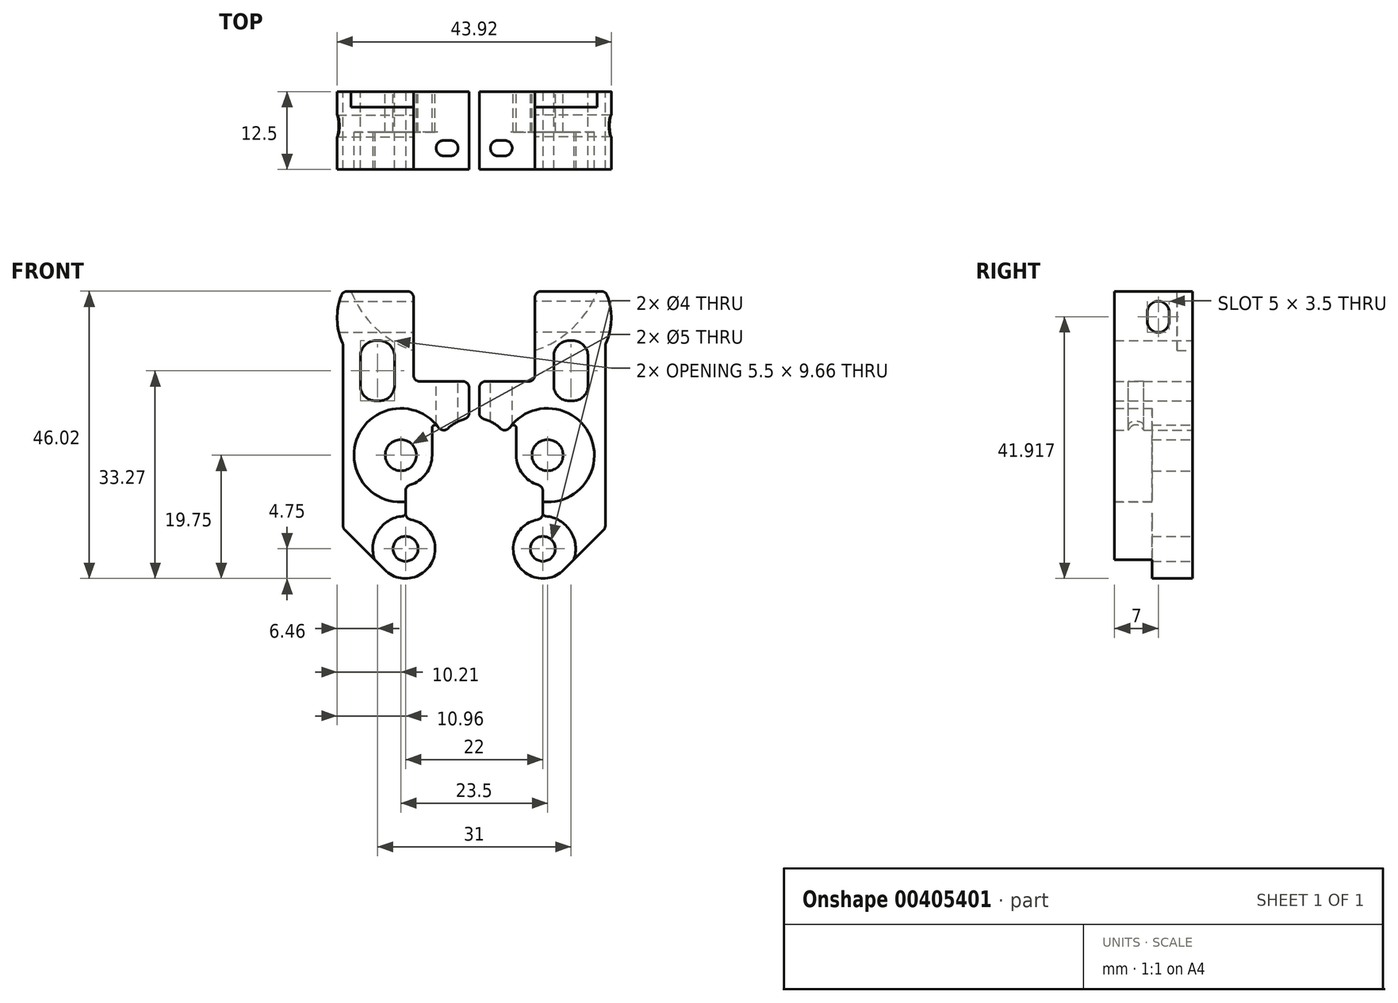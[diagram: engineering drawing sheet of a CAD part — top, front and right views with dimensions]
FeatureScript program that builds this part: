
annotation { "Feature Type Name" : "Feature", "Feature Type Description" : "" }
export const myFeature = defineFeature(function(context is Context, id is Id, definition is map)
    precondition{}
    {
        {
            var Q0;
            Q0=qCreatedBy(makeId("Front.planeOp"),FACE);
            var sketch = newSketch(context, id + "F0", { "sketchPlane" : qUnion([Q0])});
            skArc(sketch, "E0", {"start": v(6.75, 0) * mm, "mid": v(7.96, -3.26) * mm, "end": v(11, -4.94) * mm});
            skLineSegment(sketch, "E1", {"start": v(11, -4.94) * mm, "end": v(11, -10.25) * mm});
            skCircle(sketch, "E2", {"center": v(11, -15) * mm, "radius": 2 * mm});
            skArc(sketch, "E3.converted", {"start": v(11, -10.25) * mm, "mid": v(6.61, -16.82) * mm, "end": v(14.36, -18.36) * mm});
            skCircle(sketch, "E4", {"center": v(11.75, 0) * mm, "radius": 2.5 * mm});
            skPoint(sketch, "E5", {"position": v(15.5, 15.5) * mm});
            skCircle(sketch, "E6", {"center": v(15.5, 15.5) * mm, "radius": 2 * mm, "construction": true});
            skLineSegment(sketch, "E7", {"start": v(9.72, 26.27) * mm, "end": v(9.72, 11.81) * mm});
            skLineSegment(sketch, "E8", {"start": v(21, 17.74) * mm, "end": v(21, -11.72) * mm});
            skLineSegment(sketch, "E9", {"start": v(12.75, 18.35) * mm, "end": v(12.75, 8.7) * mm});
            skLineSegment(sketch, "E10", {"start": v(12.75, 8.7) * mm, "end": v(18.25, 8.7) * mm});
            skLineSegment(sketch, "E11", {"start": v(18.25, 18.35) * mm, "end": v(18.25, 8.7) * mm});
            skLineSegment(sketch, "E12", {"start": v(14.36, -18.36) * mm, "end": v(21, -11.72) * mm});
            skLineSegment(sketch, "E13", {"start": v(9.72, 26.27) * mm, "end": v(21, 26.27) * mm});
            skCircle(sketch, "E14", {"center": v(0, 0) * mm, "radius": 3.5 * mm, "construction": true});
            skLineSegment(sketch, "E15", {"start": v(4.38, 17.47) * mm, "end": v(4.38, -21.47) * mm, "construction": true});
            skLineSegment(sketch, "E16", {"start": v(3.5, 6.48) * mm, "end": v(3.5, -16.85) * mm, "construction": true});
            skLineSegment(sketch, "E17", {"start": v(5.25, 6.48) * mm, "end": v(5.25, -16.85) * mm, "construction": true});
            skLineSegment(sketch, "E18", {"start": v(0, 24.67) * mm, "end": v(0, -21.27) * mm, "construction": true});
            skLineSegment(sketch, "E19", {"start": v(0, 0) * mm, "end": v(23.5, 0) * mm, "construction": true});
            skLineSegment(sketch, "E20", {"start": v(0.79, -15) * mm, "end": v(15, -15) * mm, "construction": true});
            skCircle(sketch, "E21", {"center": v(11.75, 0) * mm, "radius": 6.5 * mm, "construction": true});
            skLineSegment(sketch, "E22", {"start": v(12.75, 18.35) * mm, "end": v(18.25, 18.35) * mm});
            skLineSegment(sketch, "E23", {"start": v(15.5, 24.97) * mm, "end": v(15.5, 6.97) * mm, "construction": true});
            skArc(sketch, "E24", {"start": v(21, 17.74) * mm, "mid": v(21.96, 22) * mm, "end": v(21, 26.27) * mm});
            skLineSegment(sketch, "E25", {"start": v(0.8, 5.95) * mm, "end": v(0.8, 11.81) * mm});
            skLineSegment(sketch, "E26", {"start": v(0.8, 11.81) * mm, "end": v(9.72, 11.81) * mm});
            skArc(sketch, "E27", {"start": v(5.01, 3.3) * mm, "mid": v(3.2, 5.08) * mm, "end": v(0.8, 5.95) * mm});
            skArc(sketch, "E28", {"start": v(6.75, 5.6) * mm, "mid": v(5.77, 4.53) * mm, "end": v(5.01, 3.3) * mm});
            skLineSegment(sketch, "E29.trimOffspring", {"start": v(6.75, 5.6) * mm, "end": v(6.75, 0) * mm});
            skSolve(sketch);
        }
        {
            var Q0;
            Q0=makeQuery(id+"F0.imprint","IMPRINT",FACE,{"disambiguationData":[TD([[makeQuery(id+"F0.imprint","IMPRINT",EDGE,{"derivedFrom":sQuery(id+"F0.wireOp",EDGE,"E0")}),1.0]])]});
            extrude(context, id + "F1", {"entities" : qUnion([Q0]), "depth" : 12.5 * mm});
        }
        {
            var Q0;
            Q0=qCreatedBy(makeId("Front.planeOp"),FACE);
            var sketch = newSketch(context, id + "F2", { "sketchPlane" : qUnion([Q0])});
            skLineSegment(sketch, "E30", {"start": v(9.72, 26.27) * mm, "end": v(19.72, 26.27) * mm});
            skLineSegment(sketch, "E31", {"start": v(9.72, 26.27) * mm, "end": v(9.72, 16.77) * mm});
            skArc(sketch, "E32", {"start": v(9.72, 16.77) * mm, "mid": v(15.8, 20.38) * mm, "end": v(19.72, 26.27) * mm});
            skSolve(sketch);
        }
        {
            var Q0;
            Q0=qSketchRegion(id+"F2",true);
            extrude(context, id + "F3", {"entities" : qUnion([Q0]), "operationType" : NewBodyOperationType.REMOVE, "depth" : 2.5 * mm});
        }
        {
            var Q0;
            Q0=makeQuery(id+"F1.opExtrude","SWEPT_FACE",FACE,{"disambiguationData":[OSD([sQuery(id+"F0.wireOp",EDGE,"E7")])]});
            var sketch = newSketch(context, id + "F4", { "sketchPlane" : qUnion([Q0])});
            skArc(sketch, "E33", {"start": v(3.75, 21.42) * mm, "mid": v(5.5, 19.67) * mm, "end": v(7.25, 21.42) * mm});
            skArc(sketch, "E34", {"start": v(7.25, 22.92) * mm, "mid": v(5.5, 24.67) * mm, "end": v(3.75, 22.92) * mm});
            skLineSegment(sketch, "E35", {"start": v(3.75, 22.92) * mm, "end": v(3.75, 21.42) * mm});
            skLineSegment(sketch, "E36", {"start": v(7.25, 22.92) * mm, "end": v(7.25, 21.42) * mm});
            skSolve(sketch);
        }
        {
            var Q0;
            Q0=qSketchRegion(id+"F4",true);
            extrude(context, id + "F5", {"entities" : qUnion([Q0]), "operationType" : NewBodyOperationType.REMOVE, "endBound" : BoundingType.THROUGH_ALL, "oppositeDirection" : true, "depth" : 25 * mm});
        }
        {
            var Q0;
            Q0=makeQuery(id+"F1.opExtrude","CAP_FACE",FACE,{"disambiguationData":[OSD([sQuery(id+"F0.wireOp",EDGE,"E0"),sQuery(id+"F0.wireOp",EDGE,"E1"),sQuery(id+"F0.wireOp",EDGE,"E2"),sQuery(id+"F0.wireOp",EDGE,"E3.converted"),sQuery(id+"F0.wireOp",EDGE,"E4"),sQuery(id+"F0.wireOp",EDGE,"OX34bXYy-n6Dd-ew0i-KdsQ-qNI713Miu0u2"),sQuery(id+"F0.wireOp",EDGE,"C01J1Lxy-QLMX-vXtg-QGuS-nqejL01fxZ92"),sQuery(id+"F0.wireOp",EDGE,"RrzfEigL-hX7B-k2Xl-mGOe-frZWyb8J06Is"),sQuery(id+"F0.wireOp",EDGE,"E7"),sQuery(id+"F0.wireOp",EDGE,"E8"),sQuery(id+"F0.wireOp",EDGE,"E9"),sQuery(id+"F0.wireOp",EDGE,"E10"),sQuery(id+"F0.wireOp",EDGE,"E11"),sQuery(id+"F0.wireOp",EDGE,"E12"),sQuery(id+"F0.wireOp",EDGE,"E13")])],"isStart":false});
            var sketch = newSketch(context, id + "F6", { "sketchPlane" : qUnion([Q0])});
            skLineSegment(sketch, "E37", {"start": v(9.72, 26.27) * mm, "end": v(9.72, 26.27) * mm});
            skArc(sketch, "E38", {"start": v(6.75, 5.6) * mm, "mid": v(18.88, 2.32) * mm, "end": v(11, -7.46) * mm});
            skArc(sketch, "E39", {"start": v(11, -9.75) * mm, "mid": v(15.3, -11.98) * mm, "end": v(15.94, -16.78) * mm});
            skLineSegment(sketch, "E40", {"start": v(11, -7.46) * mm, "end": v(11, -4.94) * mm});
            skLineSegment(sketch, "E41", {"start": v(6.75, 5.6) * mm, "end": v(6.75, 0) * mm});
            skArc(sketch, "E42", {"start": v(6.75, 0) * mm, "mid": v(7.96, -3.26) * mm, "end": v(11, -4.94) * mm});
            skLineSegment(sketch, "E43", {"start": v(11, -9.75) * mm, "end": v(11, -10.25) * mm});
            skLineSegment(sketch, "E44", {"start": v(15.94, -16.78) * mm, "end": v(14.36, -18.36) * mm});
            skArc(sketch, "E45", {"start": v(11, -10.25) * mm, "mid": v(6.61, -16.82) * mm, "end": v(14.36, -18.36) * mm});
            skSolve(sketch);
        }
        {
            var Q0;
            Q0=qSketchRegion(id+"F6",true);
            extrude(context, id + "F7", {"entities" : qUnion([Q0]), "operationType" : NewBodyOperationType.REMOVE, "oppositeDirection" : true, "depth" : 6 * mm});
        }
        {
            var Q0;
            Q0=makeQuery(id+"F1.opExtrude","SWEPT_FACE",FACE,{"disambiguationData":[OSD([sQuery(id+"F0.wireOp",EDGE,"E26")])]});
            var sketch = newSketch(context, id + "F8", { "sketchPlane" : qUnion([Q0])});
            skArc(sketch, "E46", {"start": v(3.84, -7.82) * mm, "mid": v(2.6, -9.07) * mm, "end": v(3.84, -10.32) * mm});
            skArc(sketch, "E47", {"start": v(4.84, -10.32) * mm, "mid": v(6.1, -9.07) * mm, "end": v(4.84, -7.82) * mm});
            skLineSegment(sketch, "E48", {"start": v(3.84, -7.82) * mm, "end": v(4.84, -7.82) * mm});
            skLineSegment(sketch, "E49", {"start": v(3.84, -10.32) * mm, "end": v(4.84, -10.32) * mm});
            skSolve(sketch);
        }
        {
            var Q0;
            Q0=qSketchRegion(id+"F8",true);
            extrude(context, id + "F9", {"entities" : qUnion([Q0]), "operationType" : NewBodyOperationType.REMOVE, "endBound" : BoundingType.UP_TO_NEXT, "oppositeDirection" : true, "depth" : 25 * mm});
        }
        {
            var Q0;
            Q0=makeQuery(id+"F1.opExtrude","SWEPT_BODY",BODY,{"disambiguationData":[OSD([sQuery(id+"F0.wireOp",EDGE,"E0"),sQuery(id+"F0.wireOp",EDGE,"E1"),sQuery(id+"F0.wireOp",EDGE,"E2"),sQuery(id+"F0.wireOp",EDGE,"E3.converted"),sQuery(id+"F0.wireOp",EDGE,"E4"),sQuery(id+"F0.wireOp",EDGE,"E7"),sQuery(id+"F0.wireOp",EDGE,"E8"),sQuery(id+"F0.wireOp",EDGE,"E9"),sQuery(id+"F0.wireOp",EDGE,"E10"),sQuery(id+"F0.wireOp",EDGE,"E11"),sQuery(id+"F0.wireOp",EDGE,"E12"),sQuery(id+"F0.wireOp",EDGE,"E13"),sQuery(id+"F0.wireOp",EDGE,"E22")])]});
            var Q1;
            Q1=qCreatedBy(makeId("Right.planeOp"),FACE);
            mirror(context, id + "F10", {"entities" : qUnion([Q0]), "mirrorPlane" : qUnion([Q1])});
        }
        {
            var Q0;
            Q0=makeQuery(id+"F1.opExtrude","SWEPT_EDGE",EDGE,{"disambiguationData":[OSD([sQuery(id+"F0.wireOp",EDGE,"E10"),sQuery(id+"F0.wireOp",EDGE,"E11")])]});
            var Q1;
            Q1=makeQuery(id+"F1.opExtrude","SWEPT_EDGE",EDGE,{"disambiguationData":[OSD([sQuery(id+"F0.wireOp",EDGE,"E9"),sQuery(id+"F0.wireOp",EDGE,"E10")])]});
            var Q2;
            Q2=makeQuery(id+"F1.opExtrude","SWEPT_EDGE",EDGE,{"disambiguationData":[OSD([sQuery(id+"F0.wireOp",EDGE,"E9"),sQuery(id+"F0.wireOp",EDGE,"E22")])]});
            var Q3;
            Q3=makeQuery(id+"F1.opExtrude","SWEPT_EDGE",EDGE,{"disambiguationData":[OSD([sQuery(id+"F0.wireOp",EDGE,"E11"),sQuery(id+"F0.wireOp",EDGE,"E22")])]});
            var Q4;
            Q4=makeQuery(id+"F10.opPattern","COPY",EDGE,{"derivedFrom":makeQuery(id+"F1.opExtrude","SWEPT_EDGE",EDGE,{"disambiguationData":[OSD([sQuery(id+"F0.wireOp",EDGE,"E11"),sQuery(id+"F0.wireOp",EDGE,"E22")])]}),"instanceName":"1"});
            var Q5;
            Q5=makeQuery(id+"F10.opPattern","COPY",EDGE,{"derivedFrom":makeQuery(id+"F1.opExtrude","SWEPT_EDGE",EDGE,{"disambiguationData":[OSD([sQuery(id+"F0.wireOp",EDGE,"E9"),sQuery(id+"F0.wireOp",EDGE,"E22")])]}),"instanceName":"1"});
            var Q6;
            Q6=makeQuery(id+"F10.opPattern","COPY",EDGE,{"derivedFrom":makeQuery(id+"F1.opExtrude","SWEPT_EDGE",EDGE,{"disambiguationData":[OSD([sQuery(id+"F0.wireOp",EDGE,"E10"),sQuery(id+"F0.wireOp",EDGE,"E11")])]}),"instanceName":"1"});
            var Q7;
            Q7=makeQuery(id+"F10.opPattern","COPY",EDGE,{"derivedFrom":makeQuery(id+"F1.opExtrude","SWEPT_EDGE",EDGE,{"disambiguationData":[OSD([sQuery(id+"F0.wireOp",EDGE,"E9"),sQuery(id+"F0.wireOp",EDGE,"E10")])]}),"instanceName":"1"});
            fillet(context, id + "F11", {"entities" : qUnion([Q0, Q1, Q2, Q3, Q4, Q5, Q6, Q7]), "radius" : 2.5 * mm, "tangentPropagation" : true, "allowEdgeOverflow" : false});
        }
        {
            var Q0;
            {var subQ0=sQuery(id+"F0.wireOp",EDGE,"E1");Q0=makeQuery(id+"F7.boolean.opBoolean","SPLIT",EDGE,{"disambiguationData":[topologyDisambiguationEdgeConnected([makeQuery(id+"F7.opExtrude","SWEPT_FACE",FACE,{"disambiguationData":[OSD([sQuery(id+"F6.wireOp",EDGE,"E39"),sQuery(id+"F6.wireOp",EDGE,"E45")])]})])],"derivedFrom":makeQuery(id+"F1.opExtrude","SWEPT_EDGE",EDGE,{"disambiguationData":[OSD([subQ0,sQuery(id+"F0.wireOp",EDGE,"E3.converted")])]})});}
            var Q1;
            Q1=makeQuery(id+"F1.opExtrude","SWEPT_EDGE",EDGE,{"disambiguationData":[OSD([sQuery(id+"F0.wireOp",EDGE,"E25"),sQuery(id+"F0.wireOp",EDGE,"E26")])]});
            var Q2;
            Q2=makeQuery(id+"F1.opExtrude","SWEPT_EDGE",EDGE,{"disambiguationData":[OSD([sQuery(id+"F0.wireOp",EDGE,"E7"),sQuery(id+"F0.wireOp",EDGE,"E26")])]});
            var Q3;
            {var subQ0=sQuery(id+"F0.wireOp",EDGE,"E28");var subQ1=sQuery(id+"F0.wireOp",EDGE,"E27");Q3=makeQuery(id+"F9.boolean.opBoolean","SPLIT",EDGE,{"disambiguationData":[TD([makeQuery(id+"F1.opExtrude","CAP_FACE",FACE,{"disambiguationData":[OSD([sQuery(id+"F0.wireOp",EDGE,"E0"),sQuery(id+"F0.wireOp",EDGE,"E1"),sQuery(id+"F0.wireOp",EDGE,"E2"),sQuery(id+"F0.wireOp",EDGE,"E3.converted"),sQuery(id+"F0.wireOp",EDGE,"E4"),sQuery(id+"F0.wireOp",EDGE,"E7"),sQuery(id+"F0.wireOp",EDGE,"E8"),sQuery(id+"F0.wireOp",EDGE,"E9"),sQuery(id+"F0.wireOp",EDGE,"E10"),sQuery(id+"F0.wireOp",EDGE,"E11"),sQuery(id+"F0.wireOp",EDGE,"E12"),sQuery(id+"F0.wireOp",EDGE,"E13"),sQuery(id+"F0.wireOp",EDGE,"E22"),sQuery(id+"F0.wireOp",EDGE,"E24"),sQuery(id+"F0.wireOp",EDGE,"E25"),sQuery(id+"F0.wireOp",EDGE,"E26"),subQ1,subQ0,sQuery(id+"F0.wireOp",EDGE,"E29.trimOffspring")])],"isStart":false})])],"derivedFrom":makeQuery(id+"F1.opExtrude","SWEPT_EDGE",EDGE,{"disambiguationData":[OSD([subQ1,subQ0])]})});}
            var Q4;
            {var subQ0=sQuery(id+"F0.wireOp",EDGE,"E28");var subQ1=sQuery(id+"F0.wireOp",EDGE,"E27");Q4=makeQuery(id+"F9.boolean.opBoolean","SPLIT",EDGE,{"disambiguationData":[TD([makeQuery(id+"F1.opExtrude","CAP_FACE",FACE,{"disambiguationData":[OSD([sQuery(id+"F0.wireOp",EDGE,"E0"),sQuery(id+"F0.wireOp",EDGE,"E1"),sQuery(id+"F0.wireOp",EDGE,"E2"),sQuery(id+"F0.wireOp",EDGE,"E3.converted"),sQuery(id+"F0.wireOp",EDGE,"E4"),sQuery(id+"F0.wireOp",EDGE,"E7"),sQuery(id+"F0.wireOp",EDGE,"E8"),sQuery(id+"F0.wireOp",EDGE,"E9"),sQuery(id+"F0.wireOp",EDGE,"E10"),sQuery(id+"F0.wireOp",EDGE,"E11"),sQuery(id+"F0.wireOp",EDGE,"E12"),sQuery(id+"F0.wireOp",EDGE,"E13"),sQuery(id+"F0.wireOp",EDGE,"E22"),sQuery(id+"F0.wireOp",EDGE,"E24"),sQuery(id+"F0.wireOp",EDGE,"E25"),sQuery(id+"F0.wireOp",EDGE,"E26"),subQ1,subQ0,sQuery(id+"F0.wireOp",EDGE,"E29.trimOffspring")])],"isStart":true})])],"derivedFrom":makeQuery(id+"F1.opExtrude","SWEPT_EDGE",EDGE,{"disambiguationData":[OSD([subQ1,subQ0])]})});}
            var Q5;
            Q5=makeQuery(id+"F1.opExtrude","SWEPT_EDGE",EDGE,{"disambiguationData":[OSD([sQuery(id+"F0.wireOp",EDGE,"E25"),sQuery(id+"F0.wireOp",EDGE,"E27")])]});
            var Q6;
            Q6=makeQuery(id+"F1.opExtrude","SWEPT_EDGE",EDGE,{"disambiguationData":[OSD([sQuery(id+"F0.wireOp",EDGE,"E0"),sQuery(id+"F0.wireOp",EDGE,"E1")])]});
            var Q7;
            Q7=makeQuery(id+"F7.boolean.opBoolean","COPY",EDGE,{"derivedFrom":makeQuery(id+"F7.opExtrude","SWEPT_EDGE",EDGE,{"disambiguationData":[OSD([sQuery(id+"F0.wireOp",EDGE,"E1"),sQuery(id+"F6.wireOp",EDGE,"E38"),sQuery(id+"F6.wireOp",EDGE,"E40")])]})});
            var Q8;
            Q8=makeQuery(id+"F7.boolean.opBoolean","COPY",EDGE,{"derivedFrom":makeQuery(id+"F7.opExtrude","SWEPT_EDGE",EDGE,{"disambiguationData":[OSD([sQuery(id+"F0.wireOp",EDGE,"E1"),sQuery(id+"F6.wireOp",EDGE,"E38"),sQuery(id+"F6.wireOp",EDGE,"E40")])]})});
            var Q9;
            Q9=makeQuery(id+"F1.opExtrude","SWEPT_EDGE",EDGE,{"disambiguationData":[OSD([sQuery(id+"F0.wireOp",EDGE,"E7"),sQuery(id+"F0.wireOp",EDGE,"E13")])]});
            var Q10;
            Q10=makeQuery(id+"F1.opExtrude","SWEPT_EDGE",EDGE,{"disambiguationData":[OSD([sQuery(id+"F0.wireOp",EDGE,"E13"),sQuery(id+"F0.wireOp",EDGE,"E24")])]});
            var Q11;
            Q11=makeQuery(id+"F10.opPattern","COPY",EDGE,{"derivedFrom":makeQuery(id+"F1.opExtrude","SWEPT_EDGE",EDGE,{"disambiguationData":[OSD([sQuery(id+"F0.wireOp",EDGE,"E25"),sQuery(id+"F0.wireOp",EDGE,"E26")])]}),"instanceName":"1"});
            var Q12;
            Q12=makeQuery(id+"F10.opPattern","COPY",EDGE,{"derivedFrom":makeQuery(id+"F1.opExtrude","SWEPT_EDGE",EDGE,{"disambiguationData":[OSD([sQuery(id+"F0.wireOp",EDGE,"E7"),sQuery(id+"F0.wireOp",EDGE,"E26")])]}),"instanceName":"1"});
            var Q13;
            Q13=makeQuery(id+"F10.opPattern","COPY",EDGE,{"derivedFrom":makeQuery(id+"F1.opExtrude","SWEPT_EDGE",EDGE,{"disambiguationData":[OSD([sQuery(id+"F0.wireOp",EDGE,"E7"),sQuery(id+"F0.wireOp",EDGE,"E13")])]}),"instanceName":"1"});
            var Q14;
            Q14=makeQuery(id+"F10.opPattern","COPY",EDGE,{"derivedFrom":makeQuery(id+"F1.opExtrude","SWEPT_EDGE",EDGE,{"disambiguationData":[OSD([sQuery(id+"F0.wireOp",EDGE,"E25"),sQuery(id+"F0.wireOp",EDGE,"E27")])]}),"instanceName":"1"});
            var Q15;
            {var subQ0=sQuery(id+"F0.wireOp",EDGE,"E28");var subQ1=sQuery(id+"F0.wireOp",EDGE,"E27");Q15=makeQuery(id+"F10.opPattern","COPY",EDGE,{"derivedFrom":makeQuery(id+"F9.boolean.opBoolean","SPLIT",EDGE,{"disambiguationData":[TD([makeQuery(id+"F1.opExtrude","CAP_FACE",FACE,{"disambiguationData":[OSD([sQuery(id+"F0.wireOp",EDGE,"E0"),sQuery(id+"F0.wireOp",EDGE,"E1"),sQuery(id+"F0.wireOp",EDGE,"E2"),sQuery(id+"F0.wireOp",EDGE,"E3.converted"),sQuery(id+"F0.wireOp",EDGE,"E4"),sQuery(id+"F0.wireOp",EDGE,"E7"),sQuery(id+"F0.wireOp",EDGE,"E8"),sQuery(id+"F0.wireOp",EDGE,"E9"),sQuery(id+"F0.wireOp",EDGE,"E10"),sQuery(id+"F0.wireOp",EDGE,"E11"),sQuery(id+"F0.wireOp",EDGE,"E12"),sQuery(id+"F0.wireOp",EDGE,"E13"),sQuery(id+"F0.wireOp",EDGE,"E22"),sQuery(id+"F0.wireOp",EDGE,"E24"),sQuery(id+"F0.wireOp",EDGE,"E25"),sQuery(id+"F0.wireOp",EDGE,"E26"),subQ1,subQ0,sQuery(id+"F0.wireOp",EDGE,"E29.trimOffspring")])],"isStart":true})])],"derivedFrom":makeQuery(id+"F1.opExtrude","SWEPT_EDGE",EDGE,{"disambiguationData":[OSD([subQ1,subQ0])]})}),"instanceName":"1"});}
            var Q16;
            {var subQ0=sQuery(id+"F0.wireOp",EDGE,"E28");var subQ1=sQuery(id+"F0.wireOp",EDGE,"E27");Q16=makeQuery(id+"F10.opPattern","COPY",EDGE,{"derivedFrom":makeQuery(id+"F9.boolean.opBoolean","SPLIT",EDGE,{"disambiguationData":[TD([makeQuery(id+"F1.opExtrude","CAP_FACE",FACE,{"disambiguationData":[OSD([sQuery(id+"F0.wireOp",EDGE,"E0"),sQuery(id+"F0.wireOp",EDGE,"E1"),sQuery(id+"F0.wireOp",EDGE,"E2"),sQuery(id+"F0.wireOp",EDGE,"E3.converted"),sQuery(id+"F0.wireOp",EDGE,"E4"),sQuery(id+"F0.wireOp",EDGE,"E7"),sQuery(id+"F0.wireOp",EDGE,"E8"),sQuery(id+"F0.wireOp",EDGE,"E9"),sQuery(id+"F0.wireOp",EDGE,"E10"),sQuery(id+"F0.wireOp",EDGE,"E11"),sQuery(id+"F0.wireOp",EDGE,"E12"),sQuery(id+"F0.wireOp",EDGE,"E13"),sQuery(id+"F0.wireOp",EDGE,"E22"),sQuery(id+"F0.wireOp",EDGE,"E24"),sQuery(id+"F0.wireOp",EDGE,"E25"),sQuery(id+"F0.wireOp",EDGE,"E26"),subQ1,subQ0,sQuery(id+"F0.wireOp",EDGE,"E29.trimOffspring")])],"isStart":false})])],"derivedFrom":makeQuery(id+"F1.opExtrude","SWEPT_EDGE",EDGE,{"disambiguationData":[OSD([subQ1,subQ0])]})}),"instanceName":"1"});}
            var Q17;
            Q17=makeQuery(id+"F10.opPattern","COPY",EDGE,{"derivedFrom":makeQuery(id+"F1.opExtrude","SWEPT_EDGE",EDGE,{"disambiguationData":[OSD([sQuery(id+"F0.wireOp",EDGE,"E0"),sQuery(id+"F0.wireOp",EDGE,"E1")])]}),"instanceName":"1"});
            var Q18;
            Q18=makeQuery(id+"F10.opPattern","COPY",EDGE,{"derivedFrom":makeQuery(id+"F7.boolean.opBoolean","COPY",EDGE,{"derivedFrom":makeQuery(id+"F7.opExtrude","SWEPT_EDGE",EDGE,{"disambiguationData":[OSD([sQuery(id+"F0.wireOp",EDGE,"E1"),sQuery(id+"F6.wireOp",EDGE,"E38"),sQuery(id+"F6.wireOp",EDGE,"E40")])]})}),"instanceName":"1"});
            var Q19;
            {var subQ0=sQuery(id+"F0.wireOp",EDGE,"E1");Q19=makeQuery(id+"F10.opPattern","COPY",EDGE,{"derivedFrom":makeQuery(id+"F7.boolean.opBoolean","SPLIT",EDGE,{"disambiguationData":[topologyDisambiguationEdgeConnected([makeQuery(id+"F7.opExtrude","SWEPT_FACE",FACE,{"disambiguationData":[OSD([sQuery(id+"F6.wireOp",EDGE,"E39"),sQuery(id+"F6.wireOp",EDGE,"E45")])]})])],"derivedFrom":makeQuery(id+"F1.opExtrude","SWEPT_EDGE",EDGE,{"disambiguationData":[OSD([subQ0,sQuery(id+"F0.wireOp",EDGE,"E3.converted")])]})}),"instanceName":"1"});}
            var Q20;
            Q20=makeQuery(id+"F10.opPattern","COPY",EDGE,{"derivedFrom":makeQuery(id+"F1.opExtrude","SWEPT_EDGE",EDGE,{"disambiguationData":[OSD([sQuery(id+"F0.wireOp",EDGE,"E13"),sQuery(id+"F0.wireOp",EDGE,"E24")])]}),"instanceName":"1"});
            var Q21;
            Q21=makeQuery(id+"F1.opExtrude","SWEPT_EDGE",EDGE,{"disambiguationData":[OSD([sQuery(id+"F0.wireOp",EDGE,"E8"),sQuery(id+"F0.wireOp",EDGE,"E12")])]});
            var Q22;
            Q22=makeQuery(id+"F1.opExtrude","SWEPT_EDGE",EDGE,{"disambiguationData":[OSD([sQuery(id+"F0.wireOp",EDGE,"E8"),sQuery(id+"F0.wireOp",EDGE,"E24")])]});
            var Q23;
            Q23=makeQuery(id+"F10.opPattern","COPY",EDGE,{"derivedFrom":makeQuery(id+"F1.opExtrude","SWEPT_EDGE",EDGE,{"disambiguationData":[OSD([sQuery(id+"F0.wireOp",EDGE,"E8"),sQuery(id+"F0.wireOp",EDGE,"E24")])]}),"instanceName":"1"});
            var Q24;
            Q24=makeQuery(id+"F10.opPattern","COPY",EDGE,{"derivedFrom":makeQuery(id+"F1.opExtrude","SWEPT_EDGE",EDGE,{"disambiguationData":[OSD([sQuery(id+"F0.wireOp",EDGE,"E8"),sQuery(id+"F0.wireOp",EDGE,"E12")])]}),"instanceName":"1"});
            var Q25;
            Q25=makeQuery(id+"F10.opPattern","COPY",EDGE,{"derivedFrom":makeQuery(id+"F7.boolean.opBoolean","COPY",EDGE,{"derivedFrom":makeQuery(id+"F7.opExtrude","SWEPT_EDGE",EDGE,{"disambiguationData":[OSD([sQuery(id+"F0.wireOp",EDGE,"E1"),sQuery(id+"F6.wireOp",EDGE,"E38"),sQuery(id+"F6.wireOp",EDGE,"E40")])]})}),"instanceName":"1"});
            fillet(context, id + "F12", {"entities" : qUnion([Q0, Q1, Q2, Q3, Q4, Q5, Q6, Q7, Q8, Q9, Q10, Q11, Q12, Q13, Q14, Q15, Q16, Q17, Q18, Q19, Q20, Q21, Q22, Q23, Q24, Q25]), "radius" : 1 * mm, "tangentPropagation" : true, "allowEdgeOverflow" : false});
        }
        {
            var Q0;
            Q0=makeQuery(id+"F1.opExtrude","SWEPT_EDGE",EDGE,{"disambiguationData":[OSD([sQuery(id+"F0.wireOp",EDGE,"E28"),sQuery(id+"F0.wireOp",EDGE,"E29.trimOffspring")])]});
            var Q1;
            Q1=makeQuery(id+"F10.opPattern","COPY",EDGE,{"derivedFrom":makeQuery(id+"F1.opExtrude","SWEPT_EDGE",EDGE,{"disambiguationData":[OSD([sQuery(id+"F0.wireOp",EDGE,"E28"),sQuery(id+"F0.wireOp",EDGE,"E29.trimOffspring")])]}),"instanceName":"1"});
            var Q2;
            Q2=makeQuery(id+"F3.boolean.opBoolean","COPY",EDGE,{"derivedFrom":makeQuery(id+"F3.opExtrude","SWEPT_EDGE",EDGE,{"disambiguationData":[OSD([sQuery(id+"F2.wireOp",EDGE,"E31"),sQuery(id+"F2.wireOp",EDGE,"E32")])]})});
            var Q3;
            Q3=makeQuery(id+"F3.boolean.opBoolean","COPY",EDGE,{"derivedFrom":makeQuery(id+"F3.opExtrude","SWEPT_EDGE",EDGE,{"disambiguationData":[OSD([sQuery(id+"F2.wireOp",EDGE,"E30"),sQuery(id+"F2.wireOp",EDGE,"E32")])]})});
            var Q4;
            Q4=makeQuery(id+"F10.opPattern","COPY",EDGE,{"derivedFrom":makeQuery(id+"F3.boolean.opBoolean","COPY",EDGE,{"derivedFrom":makeQuery(id+"F3.opExtrude","SWEPT_EDGE",EDGE,{"disambiguationData":[OSD([sQuery(id+"F2.wireOp",EDGE,"E31"),sQuery(id+"F2.wireOp",EDGE,"E32")])]})}),"instanceName":"1"});
            var Q5;
            Q5=makeQuery(id+"F10.opPattern","COPY",EDGE,{"derivedFrom":makeQuery(id+"F3.boolean.opBoolean","COPY",EDGE,{"derivedFrom":makeQuery(id+"F3.opExtrude","SWEPT_EDGE",EDGE,{"disambiguationData":[OSD([sQuery(id+"F2.wireOp",EDGE,"E30"),sQuery(id+"F2.wireOp",EDGE,"E32")])]})}),"instanceName":"1"});
            var Q6;
            Q6=makeQuery(id+"F7.boolean.opBoolean","COPY",EDGE,{"derivedFrom":makeQuery(id+"F7.opExtrude","SWEPT_EDGE",EDGE,{"disambiguationData":[OSD([sQuery(id+"F0.wireOp",EDGE,"E12"),sQuery(id+"F6.wireOp",EDGE,"E39"),sQuery(id+"F6.wireOp",EDGE,"E44")])]})});
            var Q7;
            Q7=makeQuery(id+"F12.opFillet","BLEND_EDGE",EDGE,{"blendedFrom":[makeQuery(id+"F1.opExtrude","SWEPT_EDGE",EDGE,{"disambiguationData":[OSD([sQuery(id+"F0.wireOp",EDGE,"E1"),sQuery(id+"F0.wireOp",EDGE,"E3.converted")])]}),makeQuery(id+"F7.boolean.opBoolean","COPY",FACE,{"derivedFrom":makeQuery(id+"F7.opExtrude","SWEPT_FACE",FACE,{"disambiguationData":[OSD([sQuery(id+"F6.wireOp",EDGE,"E39")])]})})],"blendedInto":[makeQuery(id+"F7.boolean.opBoolean","COPY",FACE,{"derivedFrom":makeQuery(id+"F7.opExtrude","SWEPT_FACE",FACE,{"disambiguationData":[OSD([sQuery(id+"F6.wireOp",EDGE,"E39")])]})})]});
            var Q8;
            Q8=makeQuery(id+"F12.opFillet","BLEND_EDGE",EDGE,{"blendedFrom":[makeQuery(id+"F10.opPattern","COPY",EDGE,{"derivedFrom":makeQuery(id+"F1.opExtrude","SWEPT_EDGE",EDGE,{"disambiguationData":[OSD([sQuery(id+"F0.wireOp",EDGE,"E1"),sQuery(id+"F0.wireOp",EDGE,"E3.converted")])]}),"instanceName":"1"}),makeQuery(id+"F10.opPattern","COPY",FACE,{"derivedFrom":makeQuery(id+"F7.boolean.opBoolean","COPY",FACE,{"derivedFrom":makeQuery(id+"F7.opExtrude","SWEPT_FACE",FACE,{"disambiguationData":[OSD([sQuery(id+"F6.wireOp",EDGE,"E39")])]})}),"instanceName":"1"})],"blendedInto":[makeQuery(id+"F10.opPattern","COPY",FACE,{"derivedFrom":makeQuery(id+"F7.boolean.opBoolean","COPY",FACE,{"derivedFrom":makeQuery(id+"F7.opExtrude","SWEPT_FACE",FACE,{"disambiguationData":[OSD([sQuery(id+"F6.wireOp",EDGE,"E39")])]})}),"instanceName":"1"})]});
            var Q9;
            Q9=makeQuery(id+"F10.opPattern","COPY",EDGE,{"derivedFrom":makeQuery(id+"F7.boolean.opBoolean","COPY",EDGE,{"derivedFrom":makeQuery(id+"F7.opExtrude","SWEPT_EDGE",EDGE,{"disambiguationData":[OSD([sQuery(id+"F0.wireOp",EDGE,"E12"),sQuery(id+"F6.wireOp",EDGE,"E39"),sQuery(id+"F6.wireOp",EDGE,"E44")])]})}),"instanceName":"1"});
            fillet(context, id + "F13", {"entities" : qUnion([Q0, Q1, Q2, Q3, Q4, Q5, Q6, Q7, Q8, Q9]), "radius" : 0.5 * mm, "tangentPropagation" : true, "allowEdgeOverflow" : false});
        }
    });
